# Revit family: Hager-VECTOR-Surface_mounted-IP65-With_Cover-With_DIN-Hosted-CH-it
name_source: partatom
category: Electrical Equipment
units: mm (PartAtom-declared; Revit-internal decimal feet)

## family parameters
Cut with Voids When Loaded = No
Host = Face
Maintain Annotation Orientation = Yes
Panel Configuration = Two Columns, Circuits Across
Part Type = Panelboard
Room Calculation Point = No
Round Connector Dimension = Use Diameter
Shared = No

## types (30) — shared parameters
BC_MODEL_ID = 1546943
BC_OBJECT_ID = 513416
BC_OBJECT_VERSION = #39
Code hager = ADD-EC000214_EU
EF000003 - modo di montaggio = apparente
EF000007 - colore = grigio
EF000024 - resistente ai raggi UV = No
EF000116 - numero RAL = 7035
EF000118 - con piastra di montaggio = No
EF001062 - versione EMC = No
EF001088 - possibilità di applicazione = Yes
EF001134 - barra DIN = Yes
EF004462 - tipo di chiusura = altri
EF005474 - grado di protezione (IP) = IP65
EF006244 - coperchio/porta trasparente = Yes
EF006306 - con serratura = No
EF015941 - porta di trasmissione del segnale = Yes
ETIM class code = EC000214
ETIM class name = Small distribution board
HG000001 - Numero di colonne = 1
HG000002-with door or cover-it = Yes
HG000003-Range-it = VECTOR
HG000005-Thickness-it = 2 mm  [stored 0.00656168 ft]
HG000006-Flush mounted-it = No
HG000009-Double swing door-it = No
HG000010-Asymmetric doors-it = No
HG000011-Empty rows from bottom-it = No
HG000012-Door swing angle-it = 90.00°
HG000013-Door on the left-it = No
HG000014-Door on the right-it = Yes
HG000015-Clearance visibility-it = Yes
HG000016-Door 3D visibility-it = Yes
HG000017-Distance between poles-it = 18 mm  [stored 0.0590551 ft]
HG000060-RAL-number = 7035
HG000099-Onfly Template ID-it-CH = 507532
Manufacturer = Hager
Name = Hager-VECTOR-Surface_mounted-IP65-With_Cover-With_DIN-NoHosted-CH-it
Name BIM&CO = Electricity
Name hager = ADD_Enclosures_EC000214
Uniformat = Low Tension Service & Dist.
Uniformat code = D501001
zero-valued in all types: Default Elevation, EF000218 - profondità di montaggio, EF000332 - altezza di installazione, EF000846 - larghezza di montaggio, EF001131 - profondità interna, HG000007-Number of empty columns-it, HG000008-Number of empty rows-it

## per-type parameters (varying)
| type | BC_VARIANT_ID | EF000008 - larghezza | EF000040 - altezza | EF000049 - profondità | EF000266 - numero di file | EF002950 - numero di unità modulari | EF009212 - tipo di coperchio | EF015776 - morsetto di messa a terra | EF015777 - morsettiera a conduttore neutro | HG000004-Manufacturer reference-it | HGEF000266-Numero di file | HGEF0002950-larghezza in unità di suddivisione |
| VECTOR-Surface_mounted_W111_H175_D93_3_Modular_Spacing-VE103A | 1173583 | 111 mm | 175 mm  [stored 0.574147 ft] | 93 mm  [stored 0.305118 ft] | 1 | 3 | chiuso | Yes | No | VE103A | 1 | 3 |
| VECTOR-Surface_mounted_W111_H175_D93_3_Modular_Spacing-VE103PN | 1173608 | 111 mm | 175 mm  [stored 0.574147 ft] | 93 mm  [stored 0.305118 ft] | 1 | 3 | con taglio | No | No | VE103PN | 1 | 3 |
| VECTOR-Surface_mounted_W111_H175_D93_3_Modular_Spacing-VE103SN | 1173626 | 111 mm | 175 mm  [stored 0.574147 ft] | 93 mm  [stored 0.305118 ft] | 1 | 3 | con taglio | No | No | VE103SN | 1 | 3 |
| VECTOR-Surface_mounted_W165_H190_D113_6_Modular_Spacing-VE106A | 1173638 | 165 mm | 190 mm | 113 mm  [stored 0.370735 ft] | 1 | 6 | chiuso | Yes | No | VE106A | 1 | 6 |
| VECTOR-Surface_mounted_W165_H190_D113_6_Modular_Spacing-VE106PN | 1173648 | 165 mm | 190 mm | 113 mm  [stored 0.370735 ft] | 1 | 6 | chiuso | No | No | VE106PN | 1 | 6 |
| VECTOR-Surface_mounted_W165_H190_D113_6_Modular_Spacing-VE106SN | 1173655 | 165 mm | 190 mm | 113 mm  [stored 0.370735 ft] | 1 | 6 | con taglio | No | No | VE106SN | 1 | 6 |
| VECTOR-Surface_mounted_W237_H210_D114_10_Modular_Spacing-VE110A | 1173657 | 237 mm  [stored 0.777559 ft] | 210 mm  [stored 0.688976 ft] | 114 mm  [stored 0.374016 ft] | 1 | 10 | chiuso | Yes | No | VE110A | 1 | 10 |
| VECTOR-Surface_mounted_W237_H210_D114_10_Modular_Spacing-VE110PN | 1173668 | 237 mm  [stored 0.777559 ft] | 210 mm  [stored 0.688976 ft] | 114 mm  [stored 0.374016 ft] | 1 | 10 | chiuso | No | No | VE110PN | 1 | 10 |
| VECTOR-Surface_mounted_W237_H210_D114_10_Modular_Spacing-VE110SN | 1173669 | 237 mm  [stored 0.777559 ft] | 210 mm  [stored 0.688976 ft] | 114 mm  [stored 0.374016 ft] | 1 | 10 | chiuso | No | No | VE110SN | 1 | 10 |
| VECTOR-Surface_mounted_W310_H302_D151_12_Modular_Spacing-VE112AK | 1173670 | 310 mm  [stored 1.01706 ft] | 302 mm  [stored 0.990814 ft] | 151 mm  [stored 0.495407 ft] | 1 | 12 | chiuso | Yes | Yes | VE112AK | 1 | 12 |
| VECTOR-Surface_mounted_W310_H302_D151_12_Modular_Spacing-VE112PN | 1173679 | 310 mm  [stored 1.01706 ft] | 302 mm  [stored 0.990814 ft] | 151 mm  [stored 0.495407 ft] | 1 | 12 | chiuso | No | No | VE112PN | 1 | 12 |
| VECTOR-Surface_mounted_W310_H302_D151_12_Modular_Spacing-VE112SN | 1173694 | 310 mm  [stored 1.01706 ft] | 302 mm  [stored 0.990814 ft] | 151 mm  [stored 0.495407 ft] | 1 | 12 | chiuso | No | No | VE112SN | 1 | 12 |
| VECTOR-Surface_mounted_W418_H302_D151_18_Modular_Spacing-VE118AK | 1173700 | 418 mm  [stored 1.37139 ft] | 302 mm  [stored 0.990814 ft] | 151 mm  [stored 0.495407 ft] | 1 | 18 | chiuso | Yes | Yes | VE118AK | 1 | 18 |
| VECTOR-Surface_mounted_W418_H302_D151_18_Modular_Spacing-VE118PN | 1173706 | 418 mm  [stored 1.37139 ft] | 302 mm  [stored 0.990814 ft] | 151 mm  [stored 0.495407 ft] | 1 | 18 | chiuso | No | No | VE118PN | 1 | 18 |
| VECTOR-Surface_mounted_W418_H302_D151_18_Modular_Spacing-VE118SN | 1173713 | 418 mm  [stored 1.37139 ft] | 302 mm  [stored 0.990814 ft] | 151 mm  [stored 0.495407 ft] | 1 | 18 | chiuso | No | No | VE118SN | 1 | 18 |
| VECTOR-Surface_mounted_W310_H427_D151_12_Modular_Spacing-VE212AK | 1173718 | 310 mm  [stored 1.01706 ft] | 427 mm  [stored 1.40092 ft] | 151 mm  [stored 0.495407 ft] | 2 | 12 | chiuso | Yes | Yes | VE212AK | 2 | 12 |
| VECTOR-Surface_mounted_W310_H427_D151_12_Modular_Spacing-VE212PN | 1173722 | 310 mm  [stored 1.01706 ft] | 427 mm  [stored 1.40092 ft] | 151 mm  [stored 0.495407 ft] | 2 | 12 | chiuso | No | No | VE212PN | 2 | 12 |
| VECTOR-Surface_mounted_W310_H427_D151_12_Modular_Spacing-VE212SN | 1173723 | 310 mm  [stored 1.01706 ft] | 427 mm  [stored 1.40092 ft] | 151 mm  [stored 0.495407 ft] | 2 | 12 | chiuso | No | No | VE212SN | 2 | 12 |
| VECTOR-Surface_mounted_W418_H452_D151_18_Modular_Spacing-VE218AK | 1173724 | 418 mm  [stored 1.37139 ft] | 452 mm  [stored 1.48294 ft] | 151 mm  [stored 0.495407 ft] | 2 | 18 | chiuso | Yes | Yes | VE218AK | 2 | 18 |
| VECTOR-Surface_mounted_W418_H452_D151_18_Modular_Spacing-VE218PN | 1173725 | 418 mm  [stored 1.37139 ft] | 452 mm  [stored 1.48294 ft] | 151 mm  [stored 0.495407 ft] | 2 | 18 | chiuso | No | No | VE218PN | 2 | 18 |
| VECTOR-Surface_mounted_W418_H452_D151_18_Modular_Spacing-VE218SN | 1173726 | 418 mm  [stored 1.37139 ft] | 452 mm  [stored 1.48294 ft] | 151 mm  [stored 0.495407 ft] | 2 | 18 | con taglio | No | No | VE218SN | 2 | 18 |
| VECTOR-Surface_mounted_W310_H552_D151_12_Modular_Spacing-VE312AK | 1173727 | 310 mm  [stored 1.01706 ft] | 552 mm  [stored 1.81102 ft] | 151 mm  [stored 0.495407 ft] | 3 | 12 | chiuso | Yes | Yes | VE312AK | 3 | 12 |
| VECTOR-Surface_mounted_W310_H552_D151_12_Modular_Spacing-VE312PN | 1173728 | 310 mm  [stored 1.01706 ft] | 552 mm  [stored 1.81102 ft] | 151 mm  [stored 0.495407 ft] | 3 | 12 | chiuso | No | No | VE312PN | 3 | 12 |
| VECTOR-Surface_mounted_W310_H552_D151_12_Modular_Spacing-VE312SN | 1173729 | 310 mm  [stored 1.01706 ft] | 552 mm  [stored 1.81102 ft] | 151 mm  [stored 0.495407 ft] | 3 | 12 | con taglio | No | No | VE312SN | 3 | 12 |
| VECTOR-Surface_mounted_W418_H602_D151_18_Modular_Spacing-VE318AK | 1173730 | 418 mm  [stored 1.37139 ft] | 602 mm  [stored 1.97507 ft] | 151 mm  [stored 0.495407 ft] | 3 | 18 | chiuso | Yes | Yes | VE318AK | 3 | 18 |
| VECTOR-Surface_mounted_W418_H602_D151_18_Modular_Spacing-VE318PN | 1173731 | 418 mm  [stored 1.37139 ft] | 602 mm  [stored 1.97507 ft] | 151 mm  [stored 0.495407 ft] | 3 | 18 | chiuso | No | No | VE318PN | 3 | 18 |
| VECTOR-Surface_mounted_W418_H602_D151_18_Modular_Spacing-VE318SN | 1173732 | 418 mm  [stored 1.37139 ft] | 602 mm  [stored 1.97507 ft] | 151 mm  [stored 0.495407 ft] | 3 | 18 | con taglio | No | No | VE318SN | 3 | 18 |
| VECTOR-Surface_mounted_W310_H677_D151_12_Modular_Spacing-VE412AK | 1173733 | 310 mm  [stored 1.01706 ft] | 677 mm  [stored 2.22113 ft] | 151 mm  [stored 0.495407 ft] | 4 | 12 | chiuso | Yes | Yes | VE412AK | 4 | 12 |
| VECTOR-Surface_mounted_W310_H677_D151_12_Modular_Spacing-VE412PN | 1173734 | 310 mm  [stored 1.01706 ft] | 677 mm  [stored 2.22113 ft] | 151 mm  [stored 0.495407 ft] | 4 | 12 | chiuso | No | No | VE412PN | 4 | 12 |
| VECTOR-Surface_mounted_W310_H677_D151_12_Modular_Spacing-VE412SN | 1173737 | 310 mm  [stored 1.01706 ft] | 677 mm  [stored 2.22113 ft] | 151 mm  [stored 0.495407 ft] | 4 | 12 | con taglio | No | No | VE412SN | 4 | 12 |

note: column(s) folded — value = type name in every type: Reference

note: [stored X ft] marks values corroborated as IEEE doubles in the binary element streams (Revit-internal decimal feet)

## geometry (parser evidence)
native form markers: Sweep x14
no freeform markers — native parametric forms only
